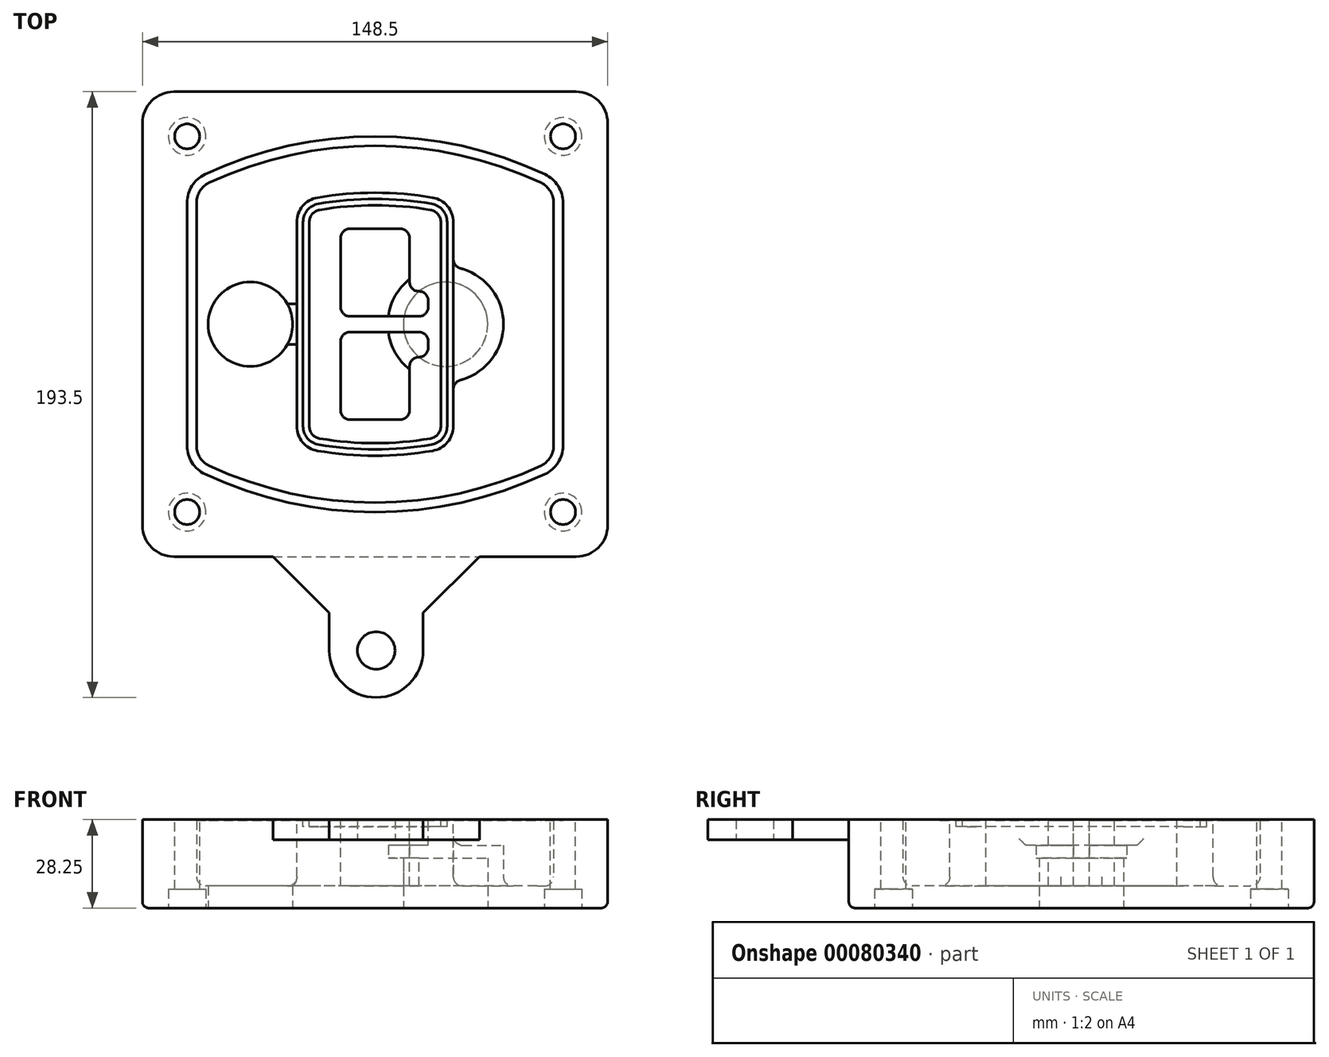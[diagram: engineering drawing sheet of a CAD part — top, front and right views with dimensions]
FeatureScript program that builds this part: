
annotation { "Feature Type Name" : "Feature", "Feature Type Description" : "" }
export const myFeature = defineFeature(function(context is Context, id is Id, definition is map)
    precondition{}
    {
        {
            var Q0;
            Q0=qCreatedBy(makeId("Top.planeOp"),FACE);
            var sketch = newSketch(context, id + "F0", { "sketchPlane" : qUnion([Q0])});
            skPoint(sketch, "E0.rect.middle", {"position": v(0, 0) * mm});
            skLineSegment(sketch, "E1.bottom", {"start": v(-64.25, -74.25) * mm, "end": v(64.25, -74.25) * mm});
            skLineSegment(sketch, "E1.top", {"start": v(-64.25, 74.25) * mm, "end": v(64.25, 74.25) * mm});
            skLineSegment(sketch, "E1.left", {"start": v(-74.25, -64.25) * mm, "end": v(-74.25, 64.25) * mm});
            skLineSegment(sketch, "E1.right", {"start": v(74.25, -64.25) * mm, "end": v(74.25, 64.25) * mm});
            skLineSegment(sketch, "E2", {"start": v(-74.25, 74.25) * mm, "end": v(74.25, -74.25) * mm, "construction": true});
            skLineSegment(sketch, "E3", {"start": v(74.25, 74.25) * mm, "end": v(-74.25, -74.25) * mm, "construction": true});
            skCircle(sketch, "E4", {"center": v(-60, 60) * mm, "radius": 4 * mm});
            skCircle(sketch, "E5", {"center": v(60, 60) * mm, "radius": 4 * mm});
            skCircle(sketch, "E6", {"center": v(60, -60) * mm, "radius": 4 * mm});
            skCircle(sketch, "E7", {"center": v(-60, -60) * mm, "radius": 4 * mm});
            skLineSegment(sketch, "E8", {"start": v(-60, 60) * mm, "end": v(60, 60) * mm, "construction": true});
            skLineSegment(sketch, "E9", {"start": v(60, 60) * mm, "end": v(60, -60) * mm, "construction": true});
            skLineSegment(sketch, "E10", {"start": v(60, -60) * mm, "end": v(-60, -60) * mm, "construction": true});
            skLineSegment(sketch, "E11", {"start": v(-60, -60) * mm, "end": v(-60, 60) * mm, "construction": true});
            skLineSegment(sketch, "E12", {"start": v(-60, 38.83) * mm, "end": v(-60, -38.83) * mm});
            skLineSegment(sketch, "E13", {"start": v(60, 38.83) * mm, "end": v(60, -38.83) * mm});
            skArc(sketch, "E14", {"start": v(54.26, 47.88) * mm, "mid": v(0, 60) * mm, "end": v(-54.26, 47.88) * mm});
            skArc(sketch, "E15", {"start": v(-54.26, -47.88) * mm, "mid": v(0, -60) * mm, "end": v(54.26, -47.88) * mm});
            skLineSegment(sketch, "E16", {"start": v(-60, 0) * mm, "end": v(60, 0) * mm, "construction": true});
            skPoint(sketch, "E17.visualSharp", {"position": v(-60, -45) * mm});
            skArc(sketch, "E17.filletArc", {"start": v(-60, -38.83) * mm, "mid": v(-58.44, -44.2) * mm, "end": v(-54.26, -47.88) * mm});
            skPoint(sketch, "E18.visualSharp", {"position": v(-60, 45) * mm});
            skArc(sketch, "E18.filletArc", {"start": v(-54.26, 47.88) * mm, "mid": v(-58.44, 44.2) * mm, "end": v(-60, 38.83) * mm});
            skPoint(sketch, "E19.visualSharp", {"position": v(60, 45) * mm});
            skArc(sketch, "E19.filletArc", {"start": v(60, 38.83) * mm, "mid": v(58.44, 44.2) * mm, "end": v(54.26, 47.88) * mm});
            skPoint(sketch, "E20.visualSharp", {"position": v(60, -45) * mm});
            skArc(sketch, "E20.filletArc", {"start": v(54.26, -47.88) * mm, "mid": v(58.44, -44.2) * mm, "end": v(60, -38.83) * mm});
            skPoint(sketch, "E21.visualSharp", {"position": v(-74.25, 74.25) * mm});
            skArc(sketch, "E21.filletArc", {"start": v(-64.25, 74.25) * mm, "mid": v(-71.32, 71.32) * mm, "end": v(-74.25, 64.25) * mm});
            skPoint(sketch, "E22.visualSharp", {"position": v(74.25, 74.25) * mm});
            skArc(sketch, "E22.filletArc", {"start": v(74.25, 64.25) * mm, "mid": v(71.32, 71.32) * mm, "end": v(64.25, 74.25) * mm});
            skPoint(sketch, "E23.visualSharp", {"position": v(74.25, -74.25) * mm});
            skArc(sketch, "E23.filletArc", {"start": v(64.25, -74.25) * mm, "mid": v(71.32, -71.32) * mm, "end": v(74.25, -64.25) * mm});
            skPoint(sketch, "E24.visualSharp", {"position": v(-74.25, -74.25) * mm});
            skArc(sketch, "E24.filletArc", {"start": v(-74.25, -64.25) * mm, "mid": v(-71.32, -71.32) * mm, "end": v(-64.25, -74.25) * mm});
            skArc(sketch, "E25.0", {"start": v(57, 38.83) * mm, "mid": v(55.9, 42.58) * mm, "end": v(52.98, 45.17) * mm});
            skLineSegment(sketch, "E25.1", {"start": v(57, 38.83) * mm, "end": v(57, -38.83) * mm});
            skArc(sketch, "E25.2", {"start": v(52.98, -45.17) * mm, "mid": v(55.9, -42.58) * mm, "end": v(57, -38.83) * mm});
            skArc(sketch, "E25.3", {"start": v(-52.98, -45.17) * mm, "mid": v(0, -57) * mm, "end": v(52.98, -45.17) * mm});
            skArc(sketch, "E25.4", {"start": v(-57, -38.83) * mm, "mid": v(-55.9, -42.58) * mm, "end": v(-52.98, -45.17) * mm});
            skArc(sketch, "E25.5", {"start": v(52.98, 45.17) * mm, "mid": v(0, 57) * mm, "end": v(-52.98, 45.17) * mm});
            skLineSegment(sketch, "E25.6", {"start": v(-57, 38.83) * mm, "end": v(-57, -38.83) * mm});
            skArc(sketch, "E25.7", {"start": v(-52.98, 45.17) * mm, "mid": v(-55.9, 42.58) * mm, "end": v(-57, 38.83) * mm});
            skArc(sketch, "E26.0", {"start": v(-55.96, 51.5) * mm, "mid": v(-61.82, 46.33) * mm, "end": v(-64, 38.83) * mm});
            skArc(sketch, "E26.1", {"start": v(55.96, 51.5) * mm, "mid": v(0, 64) * mm, "end": v(-55.96, 51.5) * mm});
            skArc(sketch, "E26.2", {"start": v(64, 38.83) * mm, "mid": v(61.82, 46.33) * mm, "end": v(55.96, 51.5) * mm});
            skLineSegment(sketch, "E26.3", {"start": v(64, 38.83) * mm, "end": v(64, -38.83) * mm});
            skArc(sketch, "E26.4", {"start": v(55.96, -51.5) * mm, "mid": v(61.82, -46.33) * mm, "end": v(64, -38.83) * mm});
            skLineSegment(sketch, "E26.5", {"start": v(-64, 38.83) * mm, "end": v(-64, -38.83) * mm});
            skArc(sketch, "E26.6", {"start": v(-55.96, -51.5) * mm, "mid": v(0, -64) * mm, "end": v(55.96, -51.5) * mm});
            skArc(sketch, "E26.7", {"start": v(-64, -38.83) * mm, "mid": v(-61.82, -46.33) * mm, "end": v(-55.96, -51.5) * mm});
            skSolve(sketch);
        }
        {
            var Q0;
            Q0=makeQuery(id+"F0.imprint","IMPRINT",FACE,{"disambiguationData":[TD([[makeQuery(id+"F0.imprint","IMPRINT",EDGE,{"derivedFrom":sQuery(id+"F0.wireOp",EDGE,"E1.bottom")}),1.0]])]});
            var Q1;
            Q1=makeQuery(id+"F0.imprint","IMPRINT",FACE,{"disambiguationData":[TD([[makeQuery(id+"F0.imprint","IMPRINT",EDGE,{"derivedFrom":sQuery(id+"F0.wireOp",EDGE,"E12")}),1.0]])]});
            var Q2;
            Q2=makeQuery(id+"F0.imprint","IMPRINT",FACE,{"disambiguationData":[TD([[makeQuery(id+"F0.imprint","IMPRINT",EDGE,{"derivedFrom":sQuery(id+"F0.wireOp",EDGE,"E25.0")}),1.0]])]});
            var Q3;
            Q3=makeQuery(id+"F0.imprint","IMPRINT",FACE,{"disambiguationData":[TD([[makeQuery(id+"F0.imprint","IMPRINT",EDGE,{"derivedFrom":sQuery(id+"F0.wireOp",EDGE,"E12")}),-1.0]])]});
            extrude(context, id + "F1", {"entities" : qUnion([Q0, Q1, Q2, Q3]), "oppositeDirection" : true, "depth" : 25 * mm});
        }
        {
            var Q0;
            Q0=makeQuery(id+"F0.imprint","IMPRINT",FACE,{"disambiguationData":[TD([[makeQuery(id+"F0.imprint","IMPRINT",EDGE,{"derivedFrom":sQuery(id+"F0.wireOp",EDGE,"E12")}),1.0]])]});
            extrude(context, id + "F2", {"entities" : qUnion([Q0]), "operationType" : NewBodyOperationType.ADD, "depth" : 3 * mm});
        }
        {
            var Q0;
            Q0=makeQuery(id+"F0.imprint","IMPRINT",FACE,{"disambiguationData":[TD([[makeQuery(id+"F0.imprint","IMPRINT",EDGE,{"derivedFrom":sQuery(id+"F0.wireOp",EDGE,"E25.0")}),1.0]])]});
            extrude(context, id + "F3", {"entities" : qUnion([Q0]), "operationType" : NewBodyOperationType.REMOVE, "oppositeDirection" : true, "depth" : 18 * mm});
        }
        {
            var Q0;
            Q0=makeQuery(id+"F2.opExtrude","CAP_FACE",FACE,{"disambiguationData":[OSD([sQuery(id+"F0.wireOp",EDGE,"E12"),sQuery(id+"F0.wireOp",EDGE,"E13"),sQuery(id+"F0.wireOp",EDGE,"E14"),sQuery(id+"F0.wireOp",EDGE,"E15"),sQuery(id+"F0.wireOp",EDGE,"E17.filletArc"),sQuery(id+"F0.wireOp",EDGE,"E18.filletArc"),sQuery(id+"F0.wireOp",EDGE,"E19.filletArc"),sQuery(id+"F0.wireOp",EDGE,"E20.filletArc"),sQuery(id+"F0.wireOp",EDGE,"E25.0"),sQuery(id+"F0.wireOp",EDGE,"E25.1"),sQuery(id+"F0.wireOp",EDGE,"E25.2"),sQuery(id+"F0.wireOp",EDGE,"E25.3"),sQuery(id+"F0.wireOp",EDGE,"E25.4"),sQuery(id+"F0.wireOp",EDGE,"E25.5"),sQuery(id+"F0.wireOp",EDGE,"E25.6"),sQuery(id+"F0.wireOp",EDGE,"E25.7")])],"isStart":false});
            var sketch = newSketch(context, id + "F4", { "sketchPlane" : qUnion([Q0])});
            skArc(sketch, "E27.0", {"start": v(-18.34, -40.45) * mm, "mid": v(0, -42) * mm, "end": v(18.34, -40.45) * mm});
            skArc(sketch, "E28.0", {"start": v(18.34, 40.45) * mm, "mid": v(0, 42) * mm, "end": v(-18.34, 40.45) * mm});
            skLineSegment(sketch, "E29", {"start": v(-25, 32.57) * mm, "end": v(-25, -32.57) * mm});
            skLineSegment(sketch, "E30", {"start": v(25, 32.57) * mm, "end": v(25, -32.57) * mm});
            skLineSegment(sketch, "E31", {"start": v(-25, 39.1) * mm, "end": v(25, 39.1) * mm, "construction": true});
            skLineSegment(sketch, "E32", {"start": v(-25, -39.1) * mm, "end": v(25, -39.1) * mm, "construction": true});
            skPoint(sketch, "E33.visualSharp", {"position": v(-25, 39.1) * mm});
            skArc(sketch, "E33.filletArc", {"start": v(-18.34, 40.45) * mm, "mid": v(-23.11, 37.73) * mm, "end": v(-25, 32.57) * mm});
            skPoint(sketch, "E34.visualSharp", {"position": v(25, 39.1) * mm});
            skArc(sketch, "E34.filletArc", {"start": v(25, 32.57) * mm, "mid": v(23.11, 37.73) * mm, "end": v(18.34, 40.45) * mm});
            skPoint(sketch, "E35.visualSharp", {"position": v(25, -39.1) * mm});
            skArc(sketch, "E35.filletArc", {"start": v(18.34, -40.45) * mm, "mid": v(23.11, -37.73) * mm, "end": v(25, -32.57) * mm});
            skPoint(sketch, "E36.visualSharp", {"position": v(-25, -39.1) * mm});
            skArc(sketch, "E36.filletArc", {"start": v(-25, -32.57) * mm, "mid": v(-23.11, -37.73) * mm, "end": v(-18.34, -40.45) * mm});
            skArc(sketch, "E37.0", {"start": v(52.98, 45.17) * mm, "mid": v(0, 57) * mm, "end": v(-52.98, 45.17) * mm});
            skArc(sketch, "E37.1", {"start": v(-52.98, 45.17) * mm, "mid": v(-55.9, 42.58) * mm, "end": v(-57, 38.83) * mm});
            skLineSegment(sketch, "E37.2", {"start": v(-57, 38.83) * mm, "end": v(-57, -38.83) * mm});
            skArc(sketch, "E37.3", {"start": v(-57, -38.83) * mm, "mid": v(-55.9, -42.58) * mm, "end": v(-52.98, -45.17) * mm});
            skArc(sketch, "E37.4", {"start": v(-52.98, -45.17) * mm, "mid": v(0, -57) * mm, "end": v(52.98, -45.17) * mm});
            skArc(sketch, "E37.5", {"start": v(52.98, -45.17) * mm, "mid": v(55.9, -42.58) * mm, "end": v(57, -38.83) * mm});
            skLineSegment(sketch, "E37.6", {"start": v(57, 38.83) * mm, "end": v(57, -38.83) * mm});
            skArc(sketch, "E37.7", {"start": v(57, 38.83) * mm, "mid": v(55.9, 42.58) * mm, "end": v(52.98, 45.17) * mm});
            skLineSegment(sketch, "E38.0", {"start": v(23, 32.57) * mm, "end": v(23, -32.57) * mm});
            skArc(sketch, "E38.1", {"start": v(18, -38.48) * mm, "mid": v(21.58, -36.44) * mm, "end": v(23, -32.57) * mm});
            skArc(sketch, "E38.2", {"start": v(-18, -38.48) * mm, "mid": v(0, -40) * mm, "end": v(18, -38.48) * mm});
            skArc(sketch, "E38.3", {"start": v(-23, -32.57) * mm, "mid": v(-21.58, -36.44) * mm, "end": v(-18, -38.48) * mm});
            skLineSegment(sketch, "E38.4", {"start": v(-23, 32.57) * mm, "end": v(-23, -32.57) * mm});
            skArc(sketch, "E38.5", {"start": v(23, 32.57) * mm, "mid": v(21.58, 36.44) * mm, "end": v(18, 38.48) * mm});
            skArc(sketch, "E38.6", {"start": v(-18, 38.48) * mm, "mid": v(-21.58, 36.44) * mm, "end": v(-23, 32.57) * mm});
            skArc(sketch, "E38.7", {"start": v(18, 38.48) * mm, "mid": v(0, 40) * mm, "end": v(-18, 38.48) * mm});
            skArc(sketch, "E39.0", {"start": v(21, 32.57) * mm, "mid": v(20.06, 35.15) * mm, "end": v(17.67, 36.5) * mm});
            skLineSegment(sketch, "E39.1", {"start": v(21, 32.57) * mm, "end": v(21, -32.57) * mm});
            skArc(sketch, "E39.2", {"start": v(17.67, -36.5) * mm, "mid": v(20.06, -35.15) * mm, "end": v(21, -32.57) * mm});
            skArc(sketch, "E39.3", {"start": v(-17.67, -36.5) * mm, "mid": v(0, -38) * mm, "end": v(17.67, -36.5) * mm});
            skArc(sketch, "E39.4", {"start": v(-21, -32.57) * mm, "mid": v(-20.06, -35.15) * mm, "end": v(-17.67, -36.5) * mm});
            skArc(sketch, "E39.5", {"start": v(17.67, 36.5) * mm, "mid": v(0, 38) * mm, "end": v(-17.67, 36.5) * mm});
            skLineSegment(sketch, "E39.6", {"start": v(-21, 32.57) * mm, "end": v(-21, -32.57) * mm});
            skArc(sketch, "E39.7", {"start": v(-17.67, 36.5) * mm, "mid": v(-20.06, 35.15) * mm, "end": v(-21, 32.57) * mm});
            skLineSegment(sketch, "E40", {"start": v(-25, 0) * mm, "end": v(25, 0) * mm, "construction": true});
            skLineSegment(sketch, "E41", {"start": v(-11, 5.5) * mm, "end": v(-11, 27.5) * mm});
            skLineSegment(sketch, "E42", {"start": v(-8, 30.5) * mm, "end": v(8, 30.5) * mm});
            skLineSegment(sketch, "E43", {"start": v(11, 27.5) * mm, "end": v(11, 13.5) * mm});
            skLineSegment(sketch, "E44", {"start": v(14, 10.5) * mm, "end": v(14, 10.5) * mm});
            skLineSegment(sketch, "E45", {"start": v(17, 7.5) * mm, "end": v(17, 5.5) * mm});
            skLineSegment(sketch, "E46", {"start": v(14, 2.5) * mm, "end": v(-8, 2.5) * mm});
            skPoint(sketch, "E47.visualSharp", {"position": v(-11, 30.5) * mm});
            skArc(sketch, "E47.filletArc", {"start": v(-8, 30.5) * mm, "mid": v(-10.12, 29.62) * mm, "end": v(-11, 27.5) * mm});
            skPoint(sketch, "E48.visualSharp", {"position": v(11, 30.5) * mm});
            skArc(sketch, "E48.filletArc", {"start": v(11, 27.5) * mm, "mid": v(10.12, 29.62) * mm, "end": v(8, 30.5) * mm});
            skPoint(sketch, "E49.visualSharp", {"position": v(11, 10.5) * mm});
            skArc(sketch, "E49.filletArc", {"start": v(11, 13.5) * mm, "mid": v(11.88, 11.38) * mm, "end": v(14, 10.5) * mm});
            skPoint(sketch, "E50.visualSharp", {"position": v(17, 10.5) * mm});
            skArc(sketch, "E50.filletArc", {"start": v(17, 7.5) * mm, "mid": v(16.12, 9.62) * mm, "end": v(14, 10.5) * mm});
            skPoint(sketch, "E51.visualSharp", {"position": v(17, 2.5) * mm});
            skArc(sketch, "E51.filletArc", {"start": v(14, 2.5) * mm, "mid": v(16.12, 3.38) * mm, "end": v(17, 5.5) * mm});
            skPoint(sketch, "E52.visualSharp", {"position": v(-11, 2.5) * mm});
            skArc(sketch, "E52.filletArc", {"start": v(-11, 5.5) * mm, "mid": v(-10.12, 3.38) * mm, "end": v(-8, 2.5) * mm});
            skLineSegment(sketch, "E53.0.MirrorCS", {"start": v(14, -2.5) * mm, "end": v(-8, -2.5) * mm});
            skArc(sketch, "E54.0.MirrorCS", {"start": v(-11, -5.5) * mm, "mid": v(-10.12, -3.38) * mm, "end": v(-8, -2.5) * mm});
            skLineSegment(sketch, "E55.0.MirrorCS", {"start": v(-11, -5.5) * mm, "end": v(-11, -27.5) * mm});
            skArc(sketch, "E56.0.MirrorCS", {"start": v(-8, -30.5) * mm, "mid": v(-10.12, -29.62) * mm, "end": v(-11, -27.5) * mm});
            skLineSegment(sketch, "E57.0.MirrorCS", {"start": v(-8, -30.5) * mm, "end": v(8, -30.5) * mm});
            skArc(sketch, "E58.0.MirrorCS", {"start": v(11, -27.5) * mm, "mid": v(10.12, -29.62) * mm, "end": v(8, -30.5) * mm});
            skLineSegment(sketch, "E59.0.MirrorCS", {"start": v(11, -27.5) * mm, "end": v(11, -13.5) * mm});
            skArc(sketch, "E60.0.MirrorCS", {"start": v(11, -13.5) * mm, "mid": v(11.88, -11.38) * mm, "end": v(14, -10.5) * mm});
            skArc(sketch, "E61.0.MirrorCS", {"start": v(17, -7.5) * mm, "mid": v(16.12, -9.62) * mm, "end": v(14, -10.5) * mm});
            skLineSegment(sketch, "E62.0.MirrorCS", {"start": v(17, -7.5) * mm, "end": v(17, -5.5) * mm});
            skArc(sketch, "E63.0.MirrorCS", {"start": v(14, -2.5) * mm, "mid": v(16.12, -3.38) * mm, "end": v(17, -5.5) * mm});
            skSolve(sketch);
        }
        {
            var Q0;
            Q0=makeQuery(id+"F4.imprint","IMPRINT",FACE,{"disambiguationData":[TD([[makeQuery(id+"F4.imprint","IMPRINT",EDGE,{"derivedFrom":sQuery(id+"F4.wireOp",EDGE,"E27.0")}),1.0]])]});
            var Q1;
            Q1=makeQuery(id+"F4.imprint","IMPRINT",FACE,{"disambiguationData":[TD([[makeQuery(id+"F4.imprint","IMPRINT",EDGE,{"derivedFrom":sQuery(id+"F4.wireOp",EDGE,"E38.0")}),-1.0]])]});
            var Q2;
            Q2=makeQuery(id+"F4.imprint","IMPRINT",FACE,{"disambiguationData":[TD([[makeQuery(id+"F4.imprint","IMPRINT",EDGE,{"derivedFrom":sQuery(id+"F4.wireOp",EDGE,"E39.0")}),1.0]])]});
            extrude(context, id + "F5", {"entities" : qUnion([Q0, Q1, Q2]), "operationType" : NewBodyOperationType.ADD, "endBound" : BoundingType.UP_TO_NEXT, "oppositeDirection" : true, "depth" : 25 * mm});
        }
        {
            var Q0;
            Q0=makeQuery(id+"F4.imprint","IMPRINT",FACE,{"disambiguationData":[TD([[makeQuery(id+"F4.imprint","IMPRINT",EDGE,{"derivedFrom":sQuery(id+"F4.wireOp",EDGE,"E38.0")}),-1.0]])]});
            extrude(context, id + "F6", {"entities" : qUnion([Q0]), "operationType" : NewBodyOperationType.REMOVE, "oppositeDirection" : true, "depth" : 2 * mm});
        }
        {
            var Q0;
            Q0=makeQuery(id+"F1.opExtrude","CAP_FACE",FACE,{"disambiguationData":[OSD([sQuery(id+"F0.wireOp",EDGE,"E1.bottom"),sQuery(id+"F0.wireOp",EDGE,"E1.top"),sQuery(id+"F0.wireOp",EDGE,"E1.left"),sQuery(id+"F0.wireOp",EDGE,"E1.right"),sQuery(id+"F0.wireOp",EDGE,"E4"),sQuery(id+"F0.wireOp",EDGE,"E5"),sQuery(id+"F0.wireOp",EDGE,"E6"),sQuery(id+"F0.wireOp",EDGE,"E7"),sQuery(id+"F0.wireOp",EDGE,"E21.filletArc"),sQuery(id+"F0.wireOp",EDGE,"E22.filletArc"),sQuery(id+"F0.wireOp",EDGE,"E23.filletArc"),sQuery(id+"F0.wireOp",EDGE,"E24.filletArc")])],"isStart":false});
            var sketch = newSketch(context, id + "F7", { "sketchPlane" : qUnion([Q0])});
            skCircle(sketch, "E64", {"center": v(22.5, 0) * mm, "radius": 13.47 * mm});
            skCircle(sketch, "E65", {"center": v(-39.81, 0) * mm, "radius": 13.47 * mm});
            skLineSegment(sketch, "E66", {"start": v(74.25, 0) * mm, "end": v(-74.25, 0) * mm});
            skCircle(sketch, "E67", {"center": v(22.5, 0) * mm, "radius": 18.47 * mm});
            skCircle(sketch, "E68", {"center": v(60, -60) * mm, "radius": 6 * mm});
            skCircle(sketch, "E69", {"center": v(-60, -60) * mm, "radius": 6 * mm});
            skCircle(sketch, "E70", {"center": v(-60, 60) * mm, "radius": 6 * mm});
            skCircle(sketch, "E71", {"center": v(60, 60) * mm, "radius": 6 * mm});
            skSolve(sketch);
        }
        {
            var Q0;
            {var subQ1=sQuery(id+"F7.wireOp",EDGE,"E66");var subQ4=sQuery(id+"F7.wireOp",EDGE,"E64");var subQ6=makeQuery(id+"F7.imprint","INTERSECT",VERTEX,{"disambiguationData":[OD(0.0)],"derivedFrom":[subQ4,subQ1]});Q0=makeQuery(id+"F7.imprint","IMPRINT",FACE,{"disambiguationData":[TD([[makeQuery(id+"F7.imprint","IMPRINT",EDGE,{"disambiguationData":[TD([[subQ6,-1.0]])],"derivedFrom":subQ4}),-1.0]])]});}
            var Q1;
            {var subQ0=sQuery(id+"F7.wireOp",EDGE,"E66");var subQ1=sQuery(id+"F7.wireOp",EDGE,"E64");var subQ3=makeQuery(id+"F7.imprint","INTERSECT",VERTEX,{"disambiguationData":[OD(0.0)],"derivedFrom":[subQ1,subQ0]});Q1=makeQuery(id+"F7.imprint","IMPRINT",FACE,{"disambiguationData":[TD([[makeQuery(id+"F7.imprint","IMPRINT",EDGE,{"disambiguationData":[TD([[subQ3,-1.0]])],"derivedFrom":subQ1}),1.0]])]});}
            var Q2;
            {var subQ0=sQuery(id+"F7.wireOp",EDGE,"E66");var subQ1=sQuery(id+"F7.wireOp",EDGE,"E64");var subQ3=makeQuery(id+"F7.imprint","INTERSECT",VERTEX,{"disambiguationData":[OD(0.0)],"derivedFrom":[subQ1,subQ0]});Q2=makeQuery(id+"F7.imprint","IMPRINT",FACE,{"disambiguationData":[TD([[makeQuery(id+"F7.imprint","IMPRINT",EDGE,{"disambiguationData":[TD([[subQ3,1.0]])],"derivedFrom":subQ1}),1.0]])]});}
            var Q3;
            {var subQ1=sQuery(id+"F7.wireOp",EDGE,"E66");var subQ4=sQuery(id+"F7.wireOp",EDGE,"E64");var subQ6=makeQuery(id+"F7.imprint","INTERSECT",VERTEX,{"disambiguationData":[OD(0.0)],"derivedFrom":[subQ4,subQ1]});Q3=makeQuery(id+"F7.imprint","IMPRINT",FACE,{"disambiguationData":[TD([[makeQuery(id+"F7.imprint","IMPRINT",EDGE,{"disambiguationData":[TD([[subQ6,1.0]])],"derivedFrom":subQ4}),-1.0]])]});}
            extrude(context, id + "F8", {"entities" : qUnion([Q0, Q1, Q2, Q3]), "operationType" : NewBodyOperationType.ADD, "oppositeDirection" : true, "depth" : 20 * mm});
        }
        {
            var Q0;
            {var subQ0=sQuery(id+"F7.wireOp",EDGE,"E66");var subQ1=sQuery(id+"F7.wireOp",EDGE,"E64");var subQ3=makeQuery(id+"F7.imprint","INTERSECT",VERTEX,{"disambiguationData":[OD(0.0)],"derivedFrom":[subQ1,subQ0]});Q0=makeQuery(id+"F7.imprint","IMPRINT",FACE,{"disambiguationData":[TD([[makeQuery(id+"F7.imprint","IMPRINT",EDGE,{"disambiguationData":[TD([[subQ3,-1.0]])],"derivedFrom":subQ1}),1.0]])]});}
            var Q1;
            {var subQ0=sQuery(id+"F7.wireOp",EDGE,"E66");var subQ1=sQuery(id+"F7.wireOp",EDGE,"E64");var subQ3=makeQuery(id+"F7.imprint","INTERSECT",VERTEX,{"disambiguationData":[OD(0.0)],"derivedFrom":[subQ1,subQ0]});Q1=makeQuery(id+"F7.imprint","IMPRINT",FACE,{"disambiguationData":[TD([[makeQuery(id+"F7.imprint","IMPRINT",EDGE,{"disambiguationData":[TD([[subQ3,1.0]])],"derivedFrom":subQ1}),1.0]])]});}
            extrude(context, id + "F9", {"entities" : qUnion([Q0, Q1]), "operationType" : NewBodyOperationType.REMOVE, "oppositeDirection" : true, "depth" : 16 * mm});
        }
        {
            var Q0;
            {var subQ0=sQuery(id+"F7.wireOp",EDGE,"E66");var subQ1=sQuery(id+"F7.wireOp",EDGE,"E65");var subQ3=makeQuery(id+"F7.imprint","INTERSECT",VERTEX,{"disambiguationData":[OD(0.0)],"derivedFrom":[subQ1,subQ0]});Q0=makeQuery(id+"F7.imprint","IMPRINT",FACE,{"disambiguationData":[TD([[makeQuery(id+"F7.imprint","IMPRINT",EDGE,{"disambiguationData":[TD([[subQ3,-1.0]])],"derivedFrom":subQ1}),1.0]])]});}
            var Q1;
            {var subQ0=sQuery(id+"F7.wireOp",EDGE,"E66");var subQ1=sQuery(id+"F7.wireOp",EDGE,"E65");var subQ3=makeQuery(id+"F7.imprint","INTERSECT",VERTEX,{"disambiguationData":[OD(0.0)],"derivedFrom":[subQ1,subQ0]});Q1=makeQuery(id+"F7.imprint","IMPRINT",FACE,{"disambiguationData":[TD([[makeQuery(id+"F7.imprint","IMPRINT",EDGE,{"disambiguationData":[TD([[subQ3,1.0]])],"derivedFrom":subQ1}),1.0]])]});}
            extrude(context, id + "F10", {"entities" : qUnion([Q0, Q1]), "operationType" : NewBodyOperationType.REMOVE, "oppositeDirection" : true, "depth" : 25 * mm});
        }
        {
            var Q0;
            Q0=makeQuery(id+"F7.imprint","IMPRINT",FACE,{"disambiguationData":[TD([[makeQuery(id+"F7.imprint","IMPRINT",EDGE,{"derivedFrom":sQuery(id+"F7.wireOp",EDGE,"E68")}),1.0]])]});
            var Q1;
            Q1=makeQuery(id+"F7.imprint","IMPRINT",FACE,{"disambiguationData":[TD([[makeQuery(id+"F7.imprint","IMPRINT",EDGE,{"derivedFrom":makeQuery(id+"F1.opExtrude","CAP_EDGE",EDGE,{"disambiguationData":[OSD([sQuery(id+"F0.wireOp",EDGE,"E5")])],"isStart":false})}),-1.0]])]});
            var Q2;
            Q2=makeQuery(id+"F7.imprint","IMPRINT",FACE,{"disambiguationData":[TD([[makeQuery(id+"F7.imprint","IMPRINT",EDGE,{"derivedFrom":sQuery(id+"F7.wireOp",EDGE,"E69")}),1.0]])]});
            var Q3;
            Q3=makeQuery(id+"F7.imprint","IMPRINT",FACE,{"disambiguationData":[TD([[makeQuery(id+"F7.imprint","IMPRINT",EDGE,{"derivedFrom":makeQuery(id+"F1.opExtrude","CAP_EDGE",EDGE,{"disambiguationData":[OSD([sQuery(id+"F0.wireOp",EDGE,"E4")])],"isStart":false})}),-1.0]])]});
            var Q4;
            Q4=makeQuery(id+"F7.imprint","IMPRINT",FACE,{"disambiguationData":[TD([[makeQuery(id+"F7.imprint","IMPRINT",EDGE,{"derivedFrom":sQuery(id+"F7.wireOp",EDGE,"E70")}),1.0]])]});
            var Q5;
            Q5=makeQuery(id+"F7.imprint","IMPRINT",FACE,{"disambiguationData":[TD([[makeQuery(id+"F7.imprint","IMPRINT",EDGE,{"derivedFrom":makeQuery(id+"F1.opExtrude","CAP_EDGE",EDGE,{"disambiguationData":[OSD([sQuery(id+"F0.wireOp",EDGE,"E7")])],"isStart":false})}),-1.0]])]});
            var Q6;
            Q6=makeQuery(id+"F7.imprint","IMPRINT",FACE,{"disambiguationData":[TD([[makeQuery(id+"F7.imprint","IMPRINT",EDGE,{"derivedFrom":sQuery(id+"F7.wireOp",EDGE,"E71")}),1.0]])]});
            var Q7;
            Q7=makeQuery(id+"F7.imprint","IMPRINT",FACE,{"disambiguationData":[TD([[makeQuery(id+"F7.imprint","IMPRINT",EDGE,{"derivedFrom":makeQuery(id+"F1.opExtrude","CAP_EDGE",EDGE,{"disambiguationData":[OSD([sQuery(id+"F0.wireOp",EDGE,"E6")])],"isStart":false})}),-1.0]])]});
            extrude(context, id + "F11", {"entities" : qUnion([Q0, Q1, Q2, Q3, Q4, Q5, Q6, Q7]), "operationType" : NewBodyOperationType.REMOVE, "oppositeDirection" : true, "depth" : 6 * mm});
        }
        {
            var Q0;
            Q0=makeQuery(id+"F9.boolean.opBoolean","COPY",FACE,{"derivedFrom":makeQuery(id+"F9.opExtrude","CAP_FACE",FACE,{"disambiguationData":[OSD([sQuery(id+"F7.wireOp",EDGE,"E64")])],"isStart":false})});
            var sketch = newSketch(context, id + "F12", { "sketchPlane" : qUnion([Q0])});
            skArc(sketch, "E72.0", {"start": v(11, 14.45) * mm, "mid": v(6.45, 9.13) * mm, "end": v(4.2, 2.5) * mm});
            skArc(sketch, "E72.1", {"start": v(4.2, -2.5) * mm, "mid": v(6.45, -9.13) * mm, "end": v(11, -14.45) * mm});
            skLineSegment(sketch, "E73", {"start": v(4.2, -2.5) * mm, "end": v(14, -2.5) * mm});
            skLineSegment(sketch, "E74.0", {"start": v(14, 2.5) * mm, "end": v(4.2, 2.5) * mm});
            skArc(sketch, "E74.1", {"start": v(14, 2.5) * mm, "mid": v(16.12, 3.38) * mm, "end": v(17, 5.5) * mm});
            skLineSegment(sketch, "E74.2", {"start": v(17, 7.5) * mm, "end": v(17, 5.5) * mm});
            skArc(sketch, "E74.3", {"start": v(17, 7.5) * mm, "mid": v(16.12, 9.62) * mm, "end": v(14, 10.5) * mm});
            skArc(sketch, "E74.4", {"start": v(11, 13.5) * mm, "mid": v(11.88, 11.38) * mm, "end": v(14, 10.5) * mm});
            skLineSegment(sketch, "E74.5", {"start": v(11, 14.45) * mm, "end": v(11, 13.5) * mm});
            skLineSegment(sketch, "E74.7", {"start": v(14, -2.5) * mm, "end": v(4.2, -2.5) * mm});
            skArc(sketch, "E74.8", {"start": v(14, -2.5) * mm, "mid": v(16.12, -3.38) * mm, "end": v(17, -5.5) * mm});
            skLineSegment(sketch, "E74.9", {"start": v(17, -7.5) * mm, "end": v(17, -5.5) * mm});
            skArc(sketch, "E74.10", {"start": v(17, -7.5) * mm, "mid": v(16.12, -9.62) * mm, "end": v(14, -10.5) * mm});
            skArc(sketch, "E74.11", {"start": v(11, -13.5) * mm, "mid": v(11.88, -11.38) * mm, "end": v(14, -10.5) * mm});
            skLineSegment(sketch, "E74.12", {"start": v(11, -14.45) * mm, "end": v(11, -13.5) * mm});
            skPoint(sketch, "E75.orphan", {"position": v(11, -27.5) * mm});
            skPoint(sketch, "E76.orphan", {"position": v(-8, -2.5) * mm});
            skPoint(sketch, "E77.orphan", {"position": v(-8, 2.5) * mm});
            skPoint(sketch, "E78.orphan", {"position": v(11, 27.5) * mm});
            skSolve(sketch);
        }
        {
            var Q0;
            {var subQ7=sQuery(id+"F12.wireOp",EDGE,"E72.0");var subQ14=sQuery(id+"F12.wireOp",EDGE,"E72.1");var subQ16=sQuery(id+"F12.wireOp",EDGE,"E74.1");var subQ18=sQuery(id+"F12.wireOp",EDGE,"E74.8");Q0=qUnion([makeQuery(id+"F12.imprint","IMPRINT",FACE,{"disambiguationData":[TD([[makeQuery(id+"F12.imprint","IMPRINT",EDGE,{"derivedFrom":subQ7}),1.0]])]}),makeQuery(id+"F12.imprint","IMPRINT",FACE,{"disambiguationData":[TD([[makeQuery(id+"F12.imprint","IMPRINT",EDGE,{"derivedFrom":subQ14}),1.0]])]}),makeQuery(id+"F12.imprint","IMPRINT",FACE,{"disambiguationData":[TD([[makeQuery(id+"F12.imprint","IMPRINT",EDGE,{"derivedFrom":subQ16}),1.0]])]}),makeQuery(id+"F12.imprint","IMPRINT",FACE,{"disambiguationData":[TD([[makeQuery(id+"F12.imprint","IMPRINT",EDGE,{"derivedFrom":subQ18}),-1.0]])]})]);}
            var Q1;
            Q1=makeQuery(id+"F5.boolean.opBoolean","SPLIT",FACE,{"disambiguationData":[TD([makeQuery(id+"F5.opExtrude","SWEPT_FACE",FACE,{"disambiguationData":[OSD([sQuery(id+"F4.wireOp",EDGE,"E41")])]})])],"derivedFrom":makeQuery(id+"F3.boolean.opBoolean","COPY",FACE,{"derivedFrom":makeQuery(id+"F3.opExtrude","CAP_FACE",FACE,{"disambiguationData":[OSD([sQuery(id+"F0.wireOp",EDGE,"E25.0"),sQuery(id+"F0.wireOp",EDGE,"E25.1"),sQuery(id+"F0.wireOp",EDGE,"E25.2"),sQuery(id+"F0.wireOp",EDGE,"E25.3"),sQuery(id+"F0.wireOp",EDGE,"E25.4"),sQuery(id+"F0.wireOp",EDGE,"E25.5"),sQuery(id+"F0.wireOp",EDGE,"E25.6"),sQuery(id+"F0.wireOp",EDGE,"E25.7")])],"isStart":false})})});
            extrude(context, id + "F13", {"entities" : qUnion([Q0]), "operationType" : NewBodyOperationType.REMOVE, "endBound" : BoundingType.UP_TO_SURFACE, "endBoundEntityFace" : qUnion([Q1]), "depth" : 25 * mm});
        }
        {
            var Q0;
            Q0=makeQuery(id+"F3.boolean.opBoolean","COPY",EDGE,{"derivedFrom":makeQuery(id+"F3.opExtrude","CAP_EDGE",EDGE,{"disambiguationData":[OSD([sQuery(id+"F0.wireOp",EDGE,"E25.6")])],"isStart":false})});
            var Q1;
            Q1=makeQuery(id+"F8.boolean.opBoolean","INTERSECT",EDGE,{"derivedFrom":[makeQuery(id+"F5.opExtrude","SWEPT_FACE",FACE,{"disambiguationData":[OSD([sQuery(id+"F4.wireOp",EDGE,"E30")])]}),makeQuery(id+"F8.opExtrude","CAP_FACE",FACE,{"disambiguationData":[OSD([sQuery(id+"F7.wireOp",EDGE,"E67")])],"isStart":false})]});
            var Q2;
            Q2=makeQuery(id+"F8.boolean.opBoolean","INTERSECT",EDGE,{"disambiguationData":[OD(1.0)],"derivedFrom":[makeQuery(id+"F5.opExtrude","SWEPT_FACE",FACE,{"disambiguationData":[OSD([sQuery(id+"F4.wireOp",EDGE,"E30")])]}),makeQuery(id+"F8.opExtrude","SWEPT_FACE",FACE,{"disambiguationData":[OSD([sQuery(id+"F7.wireOp",EDGE,"E67")])]})]});
            var Q3;
            {var subQ0=sQuery(id+"F4.wireOp",EDGE,"E30");Q3=makeQuery(id+"F8.boolean.opBoolean","SPLIT",EDGE,{"disambiguationData":[TD([makeQuery(id+"F5.opExtrude","SWEPT_FACE",FACE,{"disambiguationData":[OSD([sQuery(id+"F4.wireOp",EDGE,"E35.filletArc")])]})])],"derivedFrom":makeQuery(id+"F5.opExtrude","CAP_EDGE",EDGE,{"disambiguationData":[OSD([subQ0])],"isStart":false})});}
            var Q4;
            {var subQ0=sQuery(id+"F0.wireOp",EDGE,"E25.7");var subQ1=sQuery(id+"F0.wireOp",EDGE,"E25.1");var subQ2=sQuery(id+"F0.wireOp",EDGE,"E25.6");var subQ3=sQuery(id+"F0.wireOp",EDGE,"E25.5");var subQ4=sQuery(id+"F0.wireOp",EDGE,"E25.4");var subQ5=sQuery(id+"F0.wireOp",EDGE,"E25.0");var subQ6=sQuery(id+"F0.wireOp",EDGE,"E25.2");var subQ7=sQuery(id+"F0.wireOp",EDGE,"E25.3");Q4=makeQuery(id+"F8.boolean.opBoolean","INTERSECT",EDGE,{"derivedFrom":[makeQuery(id+"F5.boolean.opBoolean","SPLIT",FACE,{"disambiguationData":[TD([makeQuery(id+"F2.opExtrude","SWEPT_FACE",FACE,{"disambiguationData":[OSD([subQ5])]})])],"derivedFrom":makeQuery(id+"F3.boolean.opBoolean","COPY",FACE,{"derivedFrom":makeQuery(id+"F3.opExtrude","CAP_FACE",FACE,{"disambiguationData":[OSD([subQ5,subQ1,subQ6,subQ7,subQ4,subQ3,subQ2,subQ0])],"isStart":false})})}),makeQuery(id+"F8.opExtrude","SWEPT_FACE",FACE,{"disambiguationData":[OSD([sQuery(id+"F7.wireOp",EDGE,"E67")])]})]});}
            var Q5;
            Q5=makeQuery(id+"F8.boolean.opBoolean","INTERSECT",EDGE,{"disambiguationData":[OD(0.0)],"derivedFrom":[makeQuery(id+"F5.opExtrude","SWEPT_FACE",FACE,{"disambiguationData":[OSD([sQuery(id+"F4.wireOp",EDGE,"E30")])]}),makeQuery(id+"F8.opExtrude","SWEPT_FACE",FACE,{"disambiguationData":[OSD([sQuery(id+"F7.wireOp",EDGE,"E67")])]})]});
            fillet(context, id + "F14", {"entities" : qUnion([Q0, Q1, Q2, Q3, Q4, Q5]), "radius" : 3 * mm, "tangentPropagation" : true, "allowEdgeOverflow" : false});
        }
        {
            var Q0;
            Q0=makeQuery(id+"F1.opExtrude","CAP_EDGE",EDGE,{"disambiguationData":[OSD([sQuery(id+"F0.wireOp",EDGE,"E1.bottom")])],"isStart":false});
            fillet(context, id + "F15", {"entities" : qUnion([Q0]), "radius" : 2 * mm, "tangentPropagation" : true, "allowEdgeOverflow" : false});
        }
        {
            var Q0;
            {var subQ0=sQuery(id+"F0.wireOp",EDGE,"E22.filletArc");var subQ1=sQuery(id+"F0.wireOp",EDGE,"E7");var subQ2=sQuery(id+"F0.wireOp",EDGE,"E6");var subQ3=sQuery(id+"F0.wireOp",EDGE,"E5");var subQ4=sQuery(id+"F0.wireOp",EDGE,"E4");var subQ5=sQuery(id+"F0.wireOp",EDGE,"E1.bottom");var subQ6=sQuery(id+"F0.wireOp",EDGE,"E21.filletArc");var subQ7=sQuery(id+"F0.wireOp",EDGE,"E1.top");var subQ8=sQuery(id+"F0.wireOp",EDGE,"E1.left");var subQ9=sQuery(id+"F0.wireOp",EDGE,"E1.right");var subQ10=sQuery(id+"F0.wireOp",EDGE,"E23.filletArc");var subQ11=sQuery(id+"F0.wireOp",EDGE,"E24.filletArc");Q0=makeQuery(id+"F2.boolean.opBoolean","SPLIT",FACE,{"disambiguationData":[TD([makeQuery(id+"F1.opExtrude","SWEPT_FACE",FACE,{"disambiguationData":[OSD([subQ5])]})])],"derivedFrom":makeQuery(id+"F1.opExtrude","CAP_FACE",FACE,{"disambiguationData":[OSD([subQ5,subQ7,subQ8,subQ9,subQ4,subQ3,subQ2,subQ1,subQ6,subQ0,subQ10,subQ11])],"isStart":true})});}
            var sketch = newSketch(context, id + "F16", { "sketchPlane" : qUnion([Q0])});
            skArc(sketch, "E79.0", {"start": v(74.25, 64.25) * mm, "mid": v(71.32, 71.32) * mm, "end": v(64.25, 74.25) * mm});
            skLineSegment(sketch, "E79.1", {"start": v(74.25, -64.25) * mm, "end": v(74.25, 64.25) * mm});
            skLineSegment(sketch, "E79.2", {"start": v(-64.25, 74.25) * mm, "end": v(64.25, 74.25) * mm});
            skCircle(sketch, "E79.3", {"center": v(60, 60) * mm, "radius": 4 * mm});
            skCircle(sketch, "E79.4", {"center": v(60, -60) * mm, "radius": 4 * mm});
            skCircle(sketch, "E79.5", {"center": v(-60, -60) * mm, "radius": 4 * mm});
            skCircle(sketch, "E79.6", {"center": v(-60, 60) * mm, "radius": 4 * mm});
            skLineSegment(sketch, "E79.7", {"start": v(-74.25, -64.25) * mm, "end": v(-74.25, 64.25) * mm});
            skArc(sketch, "E79.8", {"start": v(-64.25, 74.25) * mm, "mid": v(-71.32, 71.32) * mm, "end": v(-74.25, 64.25) * mm});
            skArc(sketch, "E79.9", {"start": v(-74.25, -64.25) * mm, "mid": v(-71.32, -71.32) * mm, "end": v(-64.25, -74.25) * mm});
            skLineSegment(sketch, "E79.10", {"start": v(-64.25, -74.25) * mm, "end": v(64.25, -74.25) * mm});
            skArc(sketch, "E79.12", {"start": v(64.25, -74.25) * mm, "mid": v(71.32, -71.32) * mm, "end": v(74.25, -64.25) * mm});
            skArc(sketch, "E79.13", {"start": v(-54.26, -47.88) * mm, "mid": v(0, -60) * mm, "end": v(54.26, -47.88) * mm});
            skArc(sketch, "E79.14", {"start": v(54.26, -47.88) * mm, "mid": v(58.44, -44.2) * mm, "end": v(60, -38.83) * mm});
            skLineSegment(sketch, "E79.15", {"start": v(60, 38.83) * mm, "end": v(60, -38.83) * mm});
            skArc(sketch, "E79.16", {"start": v(60, 38.83) * mm, "mid": v(58.44, 44.2) * mm, "end": v(54.26, 47.88) * mm});
            skArc(sketch, "E79.17", {"start": v(54.26, 47.88) * mm, "mid": v(0, 60) * mm, "end": v(-54.26, 47.88) * mm});
            skArc(sketch, "E79.18", {"start": v(-54.26, 47.88) * mm, "mid": v(-58.44, 44.2) * mm, "end": v(-60, 38.83) * mm});
            skLineSegment(sketch, "E79.19", {"start": v(-60, 38.83) * mm, "end": v(-60, -38.83) * mm});
            skArc(sketch, "E79.20", {"start": v(-60, -38.83) * mm, "mid": v(-58.44, -44.2) * mm, "end": v(-54.26, -47.88) * mm});
            skLineSegment(sketch, "E80", {"start": v(-32.63, 74.25) * mm, "end": v(-14.63, 92.25) * mm});
            skLineSegment(sketch, "E81", {"start": v(-14.63, 92.25) * mm, "end": v(-14.63, 104.25) * mm});
            skLineSegment(sketch, "E82", {"start": v(33.37, 74.25) * mm, "end": v(15.37, 92.25) * mm});
            skLineSegment(sketch, "E83", {"start": v(15.37, 92.25) * mm, "end": v(15.37, 104.25) * mm});
            skArc(sketch, "E84", {"start": v(15.37, 104.25) * mm, "mid": v(0.37, 119.25) * mm, "end": v(-14.63, 104.25) * mm});
            skCircle(sketch, "E85", {"center": v(0.37, 104.25) * mm, "radius": 6 * mm});
            skLineSegment(sketch, "E86", {"start": v(0.37, 104.25) * mm, "end": v(0.37, 74.25) * mm, "construction": true});
            skLineSegment(sketch, "E87", {"start": v(-74.25, 0) * mm, "end": v(74.25, 0) * mm, "construction": true});
            skArc(sketch, "E88.MirrorCS", {"start": v(-14.63, 104.25) * mm, "mid": v(0.37, 119.25) * mm, "end": v(15.37, 104.25) * mm});
            skLineSegment(sketch, "E89.MirrorCS", {"start": v(-32.63, -74.25) * mm, "end": v(-14.63, -92.25) * mm});
            skLineSegment(sketch, "E90.MirrorCS", {"start": v(-14.63, -92.25) * mm, "end": v(-14.63, -104.25) * mm});
            skArc(sketch, "E91.MirrorCS", {"start": v(-14.63, -104.25) * mm, "mid": v(0.37, -119.25) * mm, "end": v(15.37, -104.25) * mm});
            skCircle(sketch, "E92.MirrorC", {"center": v(0.37, -104.25) * mm, "radius": 6 * mm});
            skLineSegment(sketch, "E93.MirrorCS", {"start": v(15.37, -92.25) * mm, "end": v(15.37, -104.25) * mm});
            skLineSegment(sketch, "E94.MirrorCS", {"start": v(33.37, -74.25) * mm, "end": v(15.37, -92.25) * mm});
            skLineSegment(sketch, "E95.MirrorCS", {"start": v(0.37, -104.25) * mm, "end": v(0.37, -74.25) * mm, "construction": true});
            skSolve(sketch);
        }
        {
            var Q0;
            {var subQ9=sQuery(id+"F16.wireOp",EDGE,"E79.0");Q0=makeQuery(id+"F16.imprint","IMPRINT",FACE,{"disambiguationData":[TD([[makeQuery(id+"F16.imprint","IMPRINT",EDGE,{"derivedFrom":subQ9}),1.0]])]});}
            var Q1;
            {var subQ1=sQuery(id+"F16.wireOp",EDGE,"E89.MirrorCS");Q1=makeQuery(id+"F16.imprint","IMPRINT",FACE,{"disambiguationData":[TD([[makeQuery(id+"F16.imprint","IMPRINT",EDGE,{"derivedFrom":subQ1}),1.0]])]});}
            var Q2;
            {var subQ0=sQuery(id+"F16.wireOp",EDGE,"E80");Q2=makeQuery(id+"F16.imprint","IMPRINT",FACE,{"disambiguationData":[TD([[makeQuery(id+"F16.imprint","IMPRINT",EDGE,{"derivedFrom":subQ0}),-1.0]])]});}
            extrude(context, id + "F17", {"entities" : qUnion([Q0, Q1, Q2]), "operationType" : NewBodyOperationType.ADD, "endBound" : BoundingType.SYMMETRIC, "depth" : 6.5 * mm});
        }
    });
